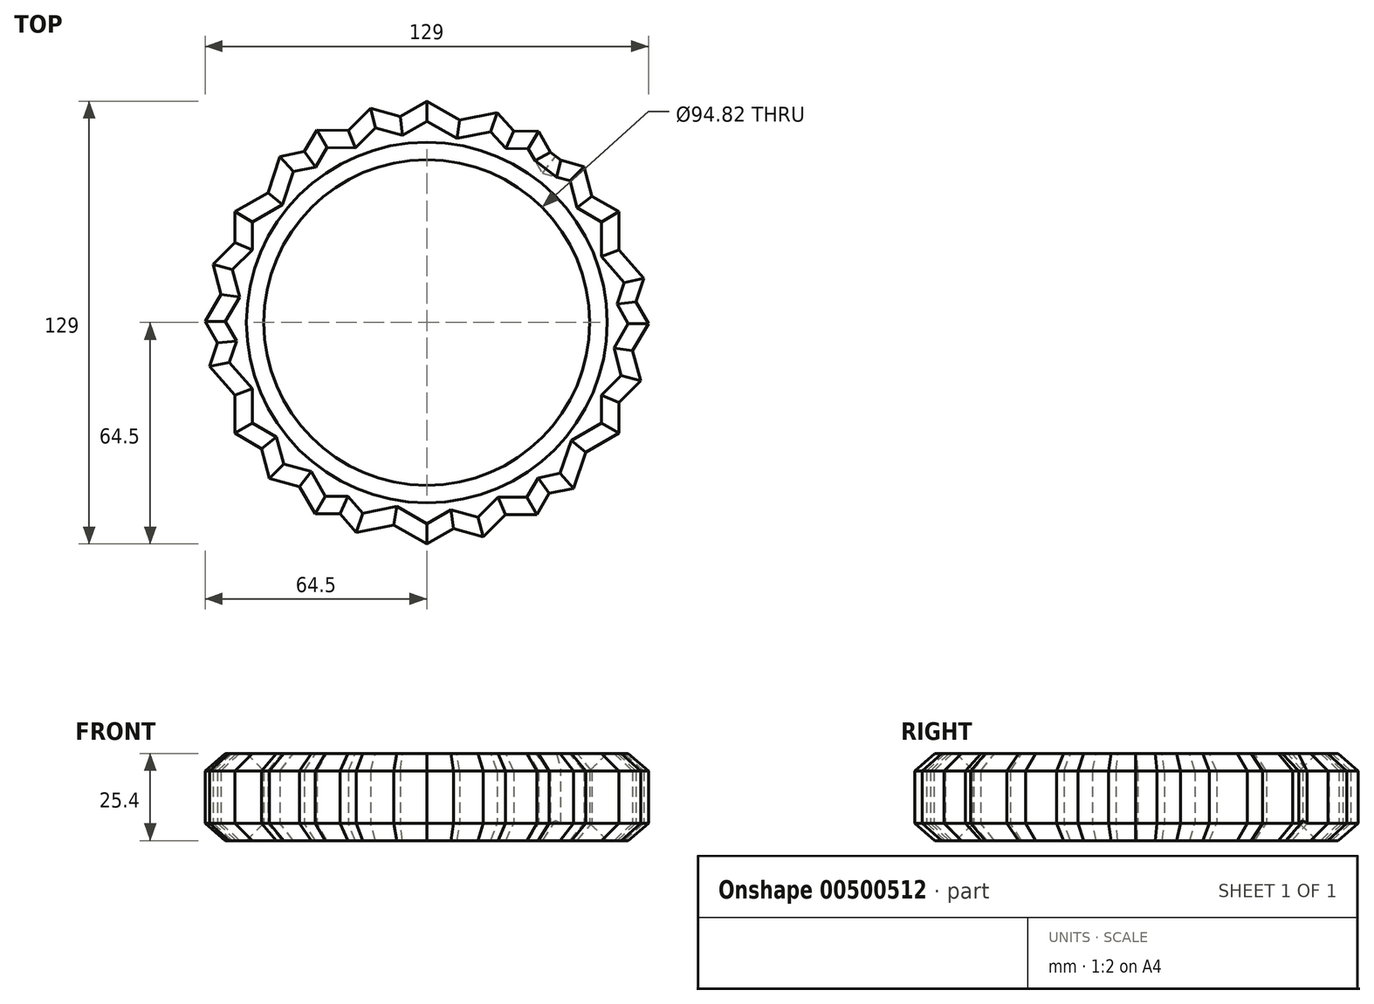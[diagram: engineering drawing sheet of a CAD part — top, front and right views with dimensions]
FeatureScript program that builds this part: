
annotation { "Feature Type Name" : "Feature", "Feature Type Description" : "" }
export const myFeature = defineFeature(function(context is Context, id is Id, definition is map)
    precondition{}
    {
        {
            var Q0;
            Q0=qCreatedBy(makeId("Top.planeOp"),FACE);
            var sketch = newSketch(context, id + "F0", { "sketchPlane" : qUnion([Q0])});
            skArc(sketch, "E0.cCircle", {"start": v(-48.24, 28.16) * mm, "mid": v(-50.87, 23.08) * mm, "end": v(-52.96, 17.76) * mm, "construction": true});
            skLineSegment(sketch, "E0.0", {"start": v(32.51, 55.7) * mm, "end": v(37.03, 47.8) * mm});
            skLineSegment(sketch, "E0.1", {"start": v(64.5, -0.3) * mm, "end": v(59.9, -8.17) * mm});
            skLineSegment(sketch, "E0.2", {"start": v(31.99, -56) * mm, "end": v(22.88, -55.97) * mm});
            skLineSegment(sketch, "E0.3", {"start": v(-32.51, -55.7) * mm, "end": v(-37.03, -47.8) * mm});
            skLineSegment(sketch, "E0.4", {"start": v(-64.5, 0.3) * mm, "end": v(-59.9, 8.17) * mm});
            skLineSegment(sketch, "E0.5", {"start": v(-31.99, 56) * mm, "end": v(-22.88, 55.97) * mm});
            skPoint(sketch, "E0.0.midPoint", {"position": v(48.5, 27.7) * mm});
            skArc(sketch, "E1.cCircle", {"start": v(-55.86, 0) * mm, "mid": v(-53.99, -14.33) * mm, "end": v(-48.5, -27.7) * mm, "construction": true});
            skLineSegment(sketch, "E1.0", {"start": v(55.86, 32.25) * mm, "end": v(55.86, 21.14) * mm});
            skLineSegment(sketch, "E1.1", {"start": v(55.86, -32.25) * mm, "end": v(46.24, -37.8) * mm});
            skLineSegment(sketch, "E1.2", {"start": v(0, -64.5) * mm, "end": v(-9.62, -58.95) * mm});
            skLineSegment(sketch, "E1.3", {"start": v(-55.86, -32.25) * mm, "end": v(-55.86, -21.14) * mm});
            skLineSegment(sketch, "E1.4", {"start": v(-55.86, 32.25) * mm, "end": v(-46.24, 37.8) * mm});
            skLineSegment(sketch, "E1.5", {"start": v(0, 64.5) * mm, "end": v(9.62, 58.95) * mm});
            skPoint(sketch, "E1.0.midPoint", {"position": v(55.86, 0) * mm});
            skArc(sketch, "E2.cCircle", {"start": v(-27.93, -48.37) * mm, "mid": v(0, -55.86) * mm, "end": v(27.93, -48.37) * mm, "construction": true});
            skLineSegment(sketch, "E2.0", {"start": v(45.82, 45.4) * mm, "end": v(48.1, 36.73) * mm});
            skLineSegment(sketch, "E2.1", {"start": v(62.22, -16.98) * mm, "end": v(55.86, -23.29) * mm});
            skLineSegment(sketch, "E2.2", {"start": v(16.4, -62.38) * mm, "end": v(7.76, -60.02) * mm});
            skLineSegment(sketch, "E2.3", {"start": v(-45.82, -45.4) * mm, "end": v(-48.1, -36.73) * mm});
            skLineSegment(sketch, "E2.4", {"start": v(-62.22, 16.98) * mm, "end": v(-55.86, 23.29) * mm});
            skLineSegment(sketch, "E2.5", {"start": v(-16.4, 62.38) * mm, "end": v(-7.76, 60.02) * mm});
            skPoint(sketch, "E2.0.midPoint", {"position": v(54.02, 14.21) * mm});
            skCircle(sketch, "E3", {"center": v(0, 0) * mm, "radius": 47.4 * mm});
            skArc(sketch, "E4.cCircle", {"start": v(-27.93, -48.37) * mm, "mid": v(7.16, -55.4) * mm, "end": v(39.32, -39.68) * mm, "construction": true});
            skLineSegment(sketch, "E4.0", {"start": v(63.21, 12.82) * mm, "end": v(60.92, 5.97) * mm});
            skLineSegment(sketch, "E4.1", {"start": v(42.7, -48.33) * mm, "end": v(35.63, -49.77) * mm});
            skLineSegment(sketch, "E4.2", {"start": v(-20.5, -61.15) * mm, "end": v(-25.29, -55.74) * mm});
            skLineSegment(sketch, "E4.3", {"start": v(-63.21, -12.82) * mm, "end": v(-60.92, -5.97) * mm});
            skLineSegment(sketch, "E4.4", {"start": v(-42.7, 48.33) * mm, "end": v(-35.63, 49.77) * mm});
            skLineSegment(sketch, "E4.5", {"start": v(20.5, 61.15) * mm, "end": v(25.29, 55.74) * mm});
            skPoint(sketch, "E4.0.midPoint", {"position": v(52.96, -17.76) * mm});
            skLineSegment(sketch, "E5.trimOffspring", {"start": v(9.62, 58.95) * mm, "end": v(20.5, 61.15) * mm});
            skLineSegment(sketch, "E6.trimOffspring", {"start": v(-35.63, 49.77) * mm, "end": v(-31.99, 56) * mm});
            skLineSegment(sketch, "E7.trimOffspring", {"start": v(-22.88, 55.97) * mm, "end": v(-16.4, 62.38) * mm});
            skLineSegment(sketch, "E8.trimOffspring", {"start": v(-7.76, 60.02) * mm, "end": v(0, 64.5) * mm});
            skLineSegment(sketch, "E9.trimOffspring", {"start": v(-46.24, 37.8) * mm, "end": v(-42.7, 48.33) * mm});
            skLineSegment(sketch, "E10.trimOffspring", {"start": v(-55.86, 23.29) * mm, "end": v(-55.86, 32.25) * mm});
            skArc(sketch, "E11.trimOffspring", {"start": v(-55.86, 0) * mm, "mid": v(-52.24, -19.77) * mm, "end": v(-41.86, -36.99) * mm, "construction": true});
            skLineSegment(sketch, "E12.trimOffspring", {"start": v(-59.9, 8.17) * mm, "end": v(-62.22, 16.98) * mm});
            skLineSegment(sketch, "E13.trimOffspring", {"start": v(-60.92, -5.97) * mm, "end": v(-64.5, 0.3) * mm});
            skLineSegment(sketch, "E14.trimOffspring", {"start": v(-55.86, -21.14) * mm, "end": v(-63.21, -12.82) * mm});
            skLineSegment(sketch, "E15.trimOffspring", {"start": v(-45.66, -32.68) * mm, "end": v(-48.5, -27.7) * mm});
            skLineSegment(sketch, "E16.trimOffspring", {"start": v(-48.1, -36.73) * mm, "end": v(-55.86, -32.25) * mm});
            skLineSegment(sketch, "E17.trimOffspring", {"start": v(-37.03, -47.8) * mm, "end": v(-45.82, -45.4) * mm});
            skLineSegment(sketch, "E18.trimOffspring", {"start": v(-25.29, -55.74) * mm, "end": v(-32.51, -55.7) * mm});
            skLineSegment(sketch, "E19.trimOffspring", {"start": v(-9.62, -58.95) * mm, "end": v(-20.5, -61.15) * mm});
            skLineSegment(sketch, "E20.trimOffspring", {"start": v(7.76, -60.02) * mm, "end": v(0, -64.5) * mm});
            skLineSegment(sketch, "E21.trimOffspring", {"start": v(22.88, -55.97) * mm, "end": v(16.4, -62.38) * mm});
            skLineSegment(sketch, "E22.trimOffspring", {"start": v(35.63, -49.77) * mm, "end": v(31.99, -56) * mm});
            skLineSegment(sketch, "E23.trimOffspring", {"start": v(39.32, -39.68) * mm, "end": v(34.19, -44.76) * mm});
            skArc(sketch, "E24.trimOffspring", {"start": v(48.24, -28.16) * mm, "mid": v(55.35, -7.55) * mm, "end": v(54.02, 14.21) * mm, "construction": true});
            skArc(sketch, "E25.trimOffspring", {"start": v(39.32, -39.68) * mm, "mid": v(47.42, -29.52) * mm, "end": v(52.96, -17.76) * mm, "construction": true});
            skLineSegment(sketch, "E26.trimOffspring", {"start": v(46.24, -37.8) * mm, "end": v(42.7, -48.33) * mm});
            skArc(sketch, "E27.trimOffspring", {"start": v(14.7, 53.89) * mm, "mid": v(-44.16, 34.2) * mm, "end": v(-48.5, -27.7) * mm, "construction": true});
            skLineSegment(sketch, "E28.trimOffspring", {"start": v(55.86, -23.29) * mm, "end": v(55.86, -32.25) * mm});
            skLineSegment(sketch, "E29.trimOffspring", {"start": v(59.9, -8.17) * mm, "end": v(62.22, -16.98) * mm});
            skLineSegment(sketch, "E30.trimOffspring", {"start": v(60.92, 5.97) * mm, "end": v(64.5, -0.3) * mm});
            skArc(sketch, "E31.trimOffspring", {"start": v(55.86, 0) * mm, "mid": v(48.37, 27.93) * mm, "end": v(27.93, 48.37) * mm, "construction": true});
            skLineSegment(sketch, "E32.trimOffspring", {"start": v(55.86, 21.14) * mm, "end": v(63.21, 12.82) * mm});
            skArc(sketch, "E33.trimOffspring", {"start": v(27.93, 48.37) * mm, "mid": v(21.5, 51.56) * mm, "end": v(14.7, 53.89) * mm, "construction": true});
            skLineSegment(sketch, "E34.trimOffspring", {"start": v(48.1, 36.73) * mm, "end": v(55.86, 32.25) * mm});
            skLineSegment(sketch, "E35.trimOffspring", {"start": v(37.03, 47.8) * mm, "end": v(45.82, 45.4) * mm});
            skLineSegment(sketch, "E36.trimOffspring", {"start": v(25.29, 55.74) * mm, "end": v(32.51, 55.7) * mm});
            skArc(sketch, "E37.trimOffspring", {"start": v(-48.24, 28.16) * mm, "mid": v(-55.86, 0.26) * mm, "end": v(-48.5, -27.7) * mm, "construction": true});
            skArc(sketch, "E38.trimOffspring", {"start": v(39.32, -39.68) * mm, "mid": v(54.02, 14.21) * mm, "end": v(14.7, 53.89) * mm, "construction": true});
            skSolve(sketch);
        }
        {
            var Q0;
            Q0 = qSketchRegion(id + "F0", true);
            extrude(context, id + "F1", {"entities" : qUnion([Q0]), "depth" : 25.4 * mm});
        }
        {
            var Q0;
            Q0=makeQuery(id+"F1.opExtrude","CAP_EDGE",EDGE,{"disambiguationData":[OSD([sQuery(id+"F0.wireOp",EDGE,"E26.trimOffspring")])],"isStart":true});
            var Q1;
            Q1=makeQuery(id+"F1.opExtrude","CAP_EDGE",EDGE,{"disambiguationData":[OSD([sQuery(id+"F0.wireOp",EDGE,"E1.1")])],"isStart":true});
            var Q2;
            Q2=makeQuery(id+"F1.opExtrude","CAP_EDGE",EDGE,{"disambiguationData":[OSD([sQuery(id+"F0.wireOp",EDGE,"E28.trimOffspring")])],"isStart":true});
            var Q3;
            Q3=makeQuery(id+"F1.opExtrude","CAP_EDGE",EDGE,{"disambiguationData":[OSD([sQuery(id+"F0.wireOp",EDGE,"E2.1")])],"isStart":true});
            var Q4;
            Q4=makeQuery(id+"F1.opExtrude","CAP_EDGE",EDGE,{"disambiguationData":[OSD([sQuery(id+"F0.wireOp",EDGE,"E0.1")])],"isStart":true});
            var Q5;
            Q5=makeQuery(id+"F1.opExtrude","CAP_EDGE",EDGE,{"disambiguationData":[OSD([sQuery(id+"F0.wireOp",EDGE,"E32.trimOffspring")])],"isStart":true});
            var Q6;
            Q6=makeQuery(id+"F1.opExtrude","CAP_EDGE",EDGE,{"disambiguationData":[OSD([sQuery(id+"F0.wireOp",EDGE,"E34.trimOffspring")])],"isStart":true});
            var Q7;
            Q7=makeQuery(id+"F1.opExtrude","CAP_EDGE",EDGE,{"disambiguationData":[OSD([sQuery(id+"F0.wireOp",EDGE,"E0.0")])],"isStart":true});
            var Q8;
            Q8=makeQuery(id+"F1.opExtrude","CAP_EDGE",EDGE,{"disambiguationData":[OSD([sQuery(id+"F0.wireOp",EDGE,"E35.trimOffspring")])],"isStart":true});
            var Q9;
            Q9=makeQuery(id+"F1.opExtrude","CAP_EDGE",EDGE,{"disambiguationData":[OSD([sQuery(id+"F0.wireOp",EDGE,"E5.trimOffspring")])],"isStart":true});
            var Q10;
            Q10=makeQuery(id+"F1.opExtrude","CAP_FACE",FACE,{"disambiguationData":[OSD([sQuery(id+"F0.wireOp",EDGE,"E0.0"),sQuery(id+"F0.wireOp",EDGE,"E0.1"),sQuery(id+"F0.wireOp",EDGE,"E0.2"),sQuery(id+"F0.wireOp",EDGE,"E0.3"),sQuery(id+"F0.wireOp",EDGE,"E0.4"),sQuery(id+"F0.wireOp",EDGE,"E0.5"),sQuery(id+"F0.wireOp",EDGE,"E1.0"),sQuery(id+"F0.wireOp",EDGE,"E1.1"),sQuery(id+"F0.wireOp",EDGE,"E1.2"),sQuery(id+"F0.wireOp",EDGE,"E1.3"),sQuery(id+"F0.wireOp",EDGE,"E1.4"),sQuery(id+"F0.wireOp",EDGE,"E1.5"),sQuery(id+"F0.wireOp",EDGE,"E2.0"),sQuery(id+"F0.wireOp",EDGE,"E2.1"),sQuery(id+"F0.wireOp",EDGE,"E2.2"),sQuery(id+"F0.wireOp",EDGE,"E2.3"),sQuery(id+"F0.wireOp",EDGE,"E2.4"),sQuery(id+"F0.wireOp",EDGE,"E2.5"),sQuery(id+"F0.wireOp",EDGE,"E3"),sQuery(id+"F0.wireOp",EDGE,"E4.0"),sQuery(id+"F0.wireOp",EDGE,"E4.1"),sQuery(id+"F0.wireOp",EDGE,"E4.2"),sQuery(id+"F0.wireOp",EDGE,"E4.3"),sQuery(id+"F0.wireOp",EDGE,"E4.4"),sQuery(id+"F0.wireOp",EDGE,"E4.5"),sQuery(id+"F0.wireOp",EDGE,"E5.trimOffspring"),sQuery(id+"F0.wireOp",EDGE,"E6.trimOffspring"),sQuery(id+"F0.wireOp",EDGE,"E7.trimOffspring"),sQuery(id+"F0.wireOp",EDGE,"E8.trimOffspring"),sQuery(id+"F0.wireOp",EDGE,"E9.trimOffspring"),sQuery(id+"F0.wireOp",EDGE,"E10.trimOffspring"),sQuery(id+"F0.wireOp",EDGE,"E12.trimOffspring"),sQuery(id+"F0.wireOp",EDGE,"E13.trimOffspring"),sQuery(id+"F0.wireOp",EDGE,"E14.trimOffspring"),sQuery(id+"F0.wireOp",EDGE,"E16.trimOffspring"),sQuery(id+"F0.wireOp",EDGE,"E17.trimOffspring"),sQuery(id+"F0.wireOp",EDGE,"E18.trimOffspring"),sQuery(id+"F0.wireOp",EDGE,"E19.trimOffspring"),sQuery(id+"F0.wireOp",EDGE,"E20.trimOffspring"),sQuery(id+"F0.wireOp",EDGE,"E21.trimOffspring"),sQuery(id+"F0.wireOp",EDGE,"E22.trimOffspring"),sQuery(id+"F0.wireOp",EDGE,"E26.trimOffspring"),sQuery(id+"F0.wireOp",EDGE,"E28.trimOffspring"),sQuery(id+"F0.wireOp",EDGE,"E29.trimOffspring"),sQuery(id+"F0.wireOp",EDGE,"E30.trimOffspring"),sQuery(id+"F0.wireOp",EDGE,"E32.trimOffspring"),sQuery(id+"F0.wireOp",EDGE,"E34.trimOffspring"),sQuery(id+"F0.wireOp",EDGE,"E35.trimOffspring"),sQuery(id+"F0.wireOp",EDGE,"E36.trimOffspring")])],"isStart":true});
            chamfer(context, id + "F2", {"entities" : qUnion([Q0, Q1, Q2, Q3, Q4, Q5, Q6, Q7, Q8, Q9, Q10]), "width" : 5.08 * mm, "tangentPropagation" : true});
        }
        {
            var Q0;
            Q0=makeQuery(id+"F1.opExtrude","CAP_EDGE",EDGE,{"disambiguationData":[OSD([sQuery(id+"F0.wireOp",EDGE,"E8.trimOffspring")])],"isStart":false});
            var Q1;
            Q1=makeQuery(id+"F1.opExtrude","CAP_EDGE",EDGE,{"disambiguationData":[OSD([sQuery(id+"F0.wireOp",EDGE,"E1.5")])],"isStart":false});
            var Q2;
            Q2=makeQuery(id+"F1.opExtrude","CAP_EDGE",EDGE,{"disambiguationData":[OSD([sQuery(id+"F0.wireOp",EDGE,"E4.5")])],"isStart":false});
            var Q3;
            Q3=makeQuery(id+"F1.opExtrude","CAP_EDGE",EDGE,{"disambiguationData":[OSD([sQuery(id+"F0.wireOp",EDGE,"E36.trimOffspring")])],"isStart":false});
            var Q4;
            Q4=makeQuery(id+"F1.opExtrude","CAP_EDGE",EDGE,{"disambiguationData":[OSD([sQuery(id+"F0.wireOp",EDGE,"E5.trimOffspring")])],"isStart":false});
            var Q5;
            Q5=makeQuery(id+"F1.opExtrude","SWEPT_EDGE",EDGE,{"disambiguationData":[OSD([sQuery(id+"F0.wireOp",EDGE,"E0.0"),sQuery(id+"F0.wireOp",EDGE,"E35.trimOffspring")])]});
            var Q6;
            Q6=makeQuery(id+"F1.opExtrude","CAP_EDGE",EDGE,{"disambiguationData":[OSD([sQuery(id+"F0.wireOp",EDGE,"E2.0")])],"isStart":false});
            var Q7;
            Q7=makeQuery(id+"F1.opExtrude","CAP_EDGE",EDGE,{"disambiguationData":[OSD([sQuery(id+"F0.wireOp",EDGE,"E34.trimOffspring")])],"isStart":false});
            var Q8;
            Q8=makeQuery(id+"F1.opExtrude","CAP_EDGE",EDGE,{"disambiguationData":[OSD([sQuery(id+"F0.wireOp",EDGE,"E1.0")])],"isStart":false});
            var Q9;
            Q9=makeQuery(id+"F1.opExtrude","CAP_EDGE",EDGE,{"disambiguationData":[OSD([sQuery(id+"F0.wireOp",EDGE,"E32.trimOffspring")])],"isStart":false});
            var Q10;
            Q10=makeQuery(id+"F1.opExtrude","CAP_EDGE",EDGE,{"disambiguationData":[OSD([sQuery(id+"F0.wireOp",EDGE,"E30.trimOffspring")])],"isStart":false});
            var Q11;
            Q11=makeQuery(id+"F1.opExtrude","CAP_EDGE",EDGE,{"disambiguationData":[OSD([sQuery(id+"F0.wireOp",EDGE,"E29.trimOffspring")])],"isStart":false});
            var Q12;
            Q12=makeQuery(id+"F1.opExtrude","CAP_EDGE",EDGE,{"disambiguationData":[OSD([sQuery(id+"F0.wireOp",EDGE,"E28.trimOffspring")])],"isStart":false});
            var Q13;
            Q13=makeQuery(id+"F1.opExtrude","CAP_EDGE",EDGE,{"disambiguationData":[OSD([sQuery(id+"F0.wireOp",EDGE,"E0.1")])],"isStart":false});
            var Q14;
            Q14=makeQuery(id+"F1.opExtrude","CAP_FACE",FACE,{"disambiguationData":[OSD([sQuery(id+"F0.wireOp",EDGE,"E0.0"),sQuery(id+"F0.wireOp",EDGE,"E0.1"),sQuery(id+"F0.wireOp",EDGE,"E0.2"),sQuery(id+"F0.wireOp",EDGE,"E0.3"),sQuery(id+"F0.wireOp",EDGE,"E0.4"),sQuery(id+"F0.wireOp",EDGE,"E0.5"),sQuery(id+"F0.wireOp",EDGE,"E1.0"),sQuery(id+"F0.wireOp",EDGE,"E1.1"),sQuery(id+"F0.wireOp",EDGE,"E1.2"),sQuery(id+"F0.wireOp",EDGE,"E1.3"),sQuery(id+"F0.wireOp",EDGE,"E1.4"),sQuery(id+"F0.wireOp",EDGE,"E1.5"),sQuery(id+"F0.wireOp",EDGE,"E2.0"),sQuery(id+"F0.wireOp",EDGE,"E2.1"),sQuery(id+"F0.wireOp",EDGE,"E2.2"),sQuery(id+"F0.wireOp",EDGE,"E2.3"),sQuery(id+"F0.wireOp",EDGE,"E2.4"),sQuery(id+"F0.wireOp",EDGE,"E2.5"),sQuery(id+"F0.wireOp",EDGE,"E3"),sQuery(id+"F0.wireOp",EDGE,"E4.0"),sQuery(id+"F0.wireOp",EDGE,"E4.1"),sQuery(id+"F0.wireOp",EDGE,"E4.2"),sQuery(id+"F0.wireOp",EDGE,"E4.3"),sQuery(id+"F0.wireOp",EDGE,"E4.4"),sQuery(id+"F0.wireOp",EDGE,"E4.5"),sQuery(id+"F0.wireOp",EDGE,"E5.trimOffspring"),sQuery(id+"F0.wireOp",EDGE,"E6.trimOffspring"),sQuery(id+"F0.wireOp",EDGE,"E7.trimOffspring"),sQuery(id+"F0.wireOp",EDGE,"E8.trimOffspring"),sQuery(id+"F0.wireOp",EDGE,"E9.trimOffspring"),sQuery(id+"F0.wireOp",EDGE,"E10.trimOffspring"),sQuery(id+"F0.wireOp",EDGE,"E12.trimOffspring"),sQuery(id+"F0.wireOp",EDGE,"E13.trimOffspring"),sQuery(id+"F0.wireOp",EDGE,"E14.trimOffspring"),sQuery(id+"F0.wireOp",EDGE,"E16.trimOffspring"),sQuery(id+"F0.wireOp",EDGE,"E17.trimOffspring"),sQuery(id+"F0.wireOp",EDGE,"E18.trimOffspring"),sQuery(id+"F0.wireOp",EDGE,"E19.trimOffspring"),sQuery(id+"F0.wireOp",EDGE,"E20.trimOffspring"),sQuery(id+"F0.wireOp",EDGE,"E21.trimOffspring"),sQuery(id+"F0.wireOp",EDGE,"E22.trimOffspring"),sQuery(id+"F0.wireOp",EDGE,"E26.trimOffspring"),sQuery(id+"F0.wireOp",EDGE,"E28.trimOffspring"),sQuery(id+"F0.wireOp",EDGE,"E29.trimOffspring"),sQuery(id+"F0.wireOp",EDGE,"E30.trimOffspring"),sQuery(id+"F0.wireOp",EDGE,"E32.trimOffspring"),sQuery(id+"F0.wireOp",EDGE,"E34.trimOffspring"),sQuery(id+"F0.wireOp",EDGE,"E35.trimOffspring"),sQuery(id+"F0.wireOp",EDGE,"E36.trimOffspring")])],"isStart":false});
            chamfer(context, id + "F3", {"entities" : qUnion([Q0, Q1, Q2, Q3, Q4, Q5, Q6, Q7, Q8, Q9, Q10, Q11, Q12, Q13, Q14]), "width" : 5.08 * mm, "tangentPropagation" : true});
        }
    });
